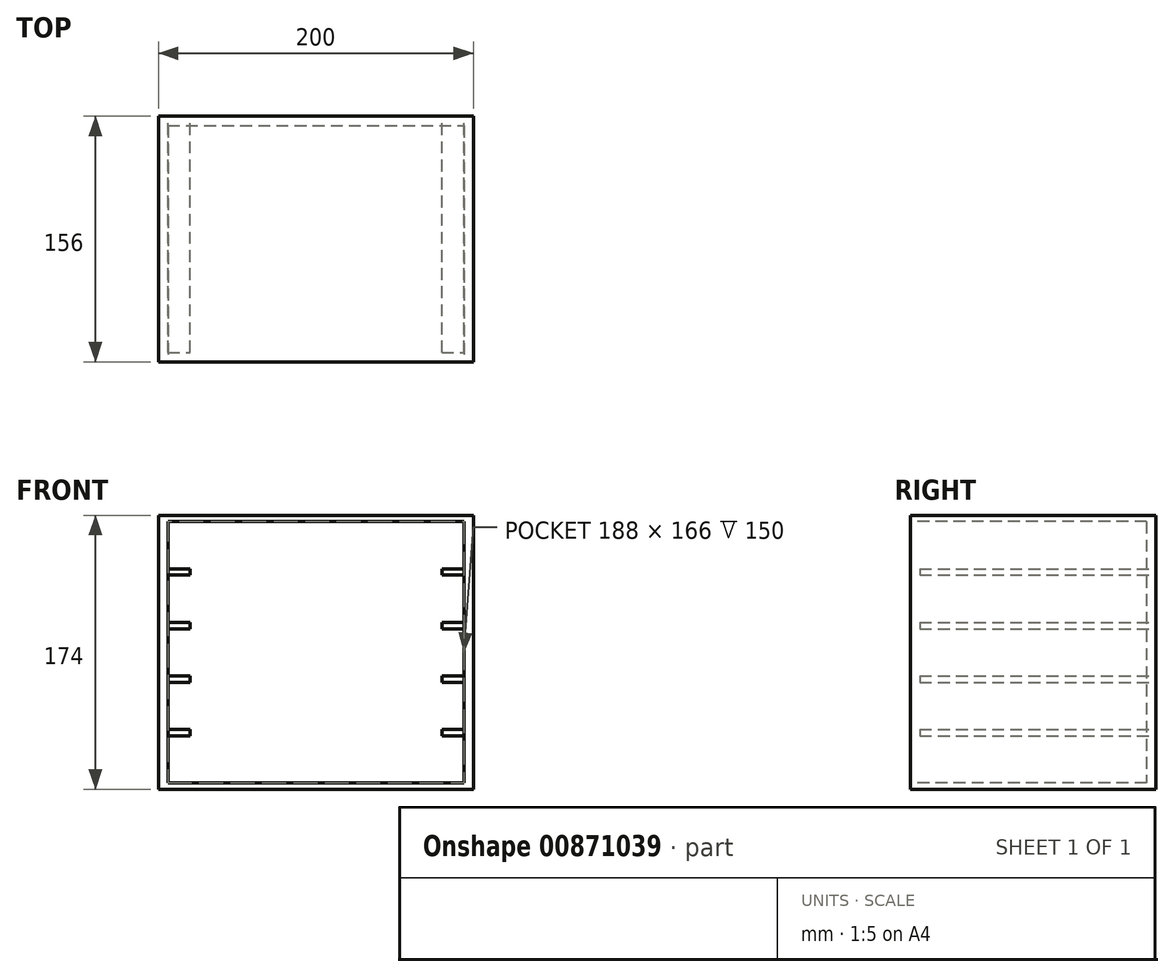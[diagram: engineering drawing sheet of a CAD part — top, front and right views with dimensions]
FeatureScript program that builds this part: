
annotation { "Feature Type Name" : "Feature", "Feature Type Description" : "" }
export const myFeature = defineFeature(function(context is Context, id is Id, definition is map)
    precondition{}
    {
        {
            var Q0;
            Q0=qCreatedBy(makeId("Front.planeOp"),FACE);
            var sketch = newSketch(context, id + "F0", { "sketchPlane" : qUnion([Q0])});
            skLineSegment(sketch, "E0.bottom", {"start": v(-100, 87) * mm, "end": v(100, 87) * mm});
            skLineSegment(sketch, "E0.top", {"start": v(-100, -87) * mm, "end": v(100, -87) * mm});
            skLineSegment(sketch, "E0.left", {"start": v(-100, 87) * mm, "end": v(-100, -87) * mm});
            skLineSegment(sketch, "E0.right", {"start": v(100, 87) * mm, "end": v(100, -87) * mm});
            skSolve(sketch);
        }
        {
            var Q0;
            Q0=makeQuery(id+"F0.imprint","IMPRINT",FACE,{"disambiguationData":[TD([[makeQuery(id+"F0.imprint","IMPRINT",EDGE,{"derivedFrom":sQuery(id+"F0.wireOp",EDGE,"E0.bottom")}),-1.0]])]});
            extrude(context, id + "F1", {"entities" : qUnion([Q0]), "depth" : 156 * mm, "offsetDistance" : 25 * mm});
        }
        {
            var Q0;
            Q0=makeQuery(id+"F1.opExtrude","CAP_FACE",FACE,{"disambiguationData":[OSD([sQuery(id+"F0.wireOp",EDGE,"E0.bottom"),sQuery(id+"F0.wireOp",EDGE,"E0.top"),sQuery(id+"F0.wireOp",EDGE,"E0.left"),sQuery(id+"F0.wireOp",EDGE,"E0.right")])],"isStart":false});
            var sketch = newSketch(context, id + "F2", { "sketchPlane" : qUnion([Q0])});
            skLineSegment(sketch, "E1.bottom", {"start": v(-94, 83) * mm, "end": v(94, 83) * mm});
            skLineSegment(sketch, "E1.top", {"start": v(-94, -83) * mm, "end": v(94, -83) * mm});
            skLineSegment(sketch, "E1.left", {"start": v(-94, 83) * mm, "end": v(-94, -83) * mm});
            skLineSegment(sketch, "E1.right", {"start": v(94, 83) * mm, "end": v(94, -83) * mm});
            skSolve(sketch);
        }
        {
            var Q0;
            Q0 = qSketchRegion(id + "F2", true);
            extrude(context, id + "F3", {"entities" : qUnion([Q0]), "operationType" : NewBodyOperationType.REMOVE, "oppositeDirection" : true, "depth" : 150 * mm, "offsetDistance" : 25 * mm});
        }
        {
            var Q0;
            Q0=qCreatedBy(makeId("Front.planeOp"),FACE);
            var sketch = newSketch(context, id + "F4", { "sketchPlane" : qUnion([Q0])});
            skLineSegment(sketch, "E2.bottom", {"start": v(-94, 83) * mm, "end": v(94, 83) * mm});
            skLineSegment(sketch, "E2.top", {"start": v(-94, -83) * mm, "end": v(94, -83) * mm});
            skLineSegment(sketch, "E2.left", {"start": v(-94, 83) * mm, "end": v(-94, -83) * mm});
            skLineSegment(sketch, "E2.right", {"start": v(94, 83) * mm, "end": v(94, -83) * mm});
            skLineSegment(sketch, "E3.bottom", {"start": v(-94, -83) * mm, "end": v(-80, -83) * mm});
            skLineSegment(sketch, "E3.top", {"start": v(-94, -87) * mm, "end": v(-80, -87) * mm});
            skLineSegment(sketch, "E3.left", {"start": v(-94, -83) * mm, "end": v(-94, -87) * mm});
            skLineSegment(sketch, "E3.right", {"start": v(-80, -83) * mm, "end": v(-80, -87) * mm});
            skLineSegment(sketch, "E4.0.1.0", {"start": v(-94, -53) * mm, "end": v(-80, -53) * mm});
            skLineSegment(sketch, "E4.0.1.1", {"start": v(-80, -49) * mm, "end": v(-80, -53) * mm});
            skLineSegment(sketch, "E4.0.1.2", {"start": v(-94, -49) * mm, "end": v(-80, -49) * mm});
            skLineSegment(sketch, "E4.0.1.3", {"start": v(-94, -49) * mm, "end": v(-94, -53) * mm});
            skLineSegment(sketch, "E4.0.2.0", {"start": v(-94, -19) * mm, "end": v(-80, -19) * mm});
            skLineSegment(sketch, "E4.0.2.1", {"start": v(-80, -15) * mm, "end": v(-80, -19) * mm});
            skLineSegment(sketch, "E4.0.2.2", {"start": v(-94, -15) * mm, "end": v(-80, -15) * mm});
            skLineSegment(sketch, "E4.0.2.3", {"start": v(-94, -15) * mm, "end": v(-94, -19) * mm});
            skLineSegment(sketch, "E4.0.3.0", {"start": v(-94, 15) * mm, "end": v(-80, 15) * mm});
            skLineSegment(sketch, "E4.0.3.1", {"start": v(-80, 19) * mm, "end": v(-80, 15) * mm});
            skLineSegment(sketch, "E4.0.3.2", {"start": v(-94, 19) * mm, "end": v(-80, 19) * mm});
            skLineSegment(sketch, "E4.0.3.3", {"start": v(-94, 19) * mm, "end": v(-94, 15) * mm});
            skLineSegment(sketch, "E4.0.4.0", {"start": v(-94, 49) * mm, "end": v(-80, 49) * mm});
            skLineSegment(sketch, "E4.0.4.1", {"start": v(-80, 53) * mm, "end": v(-80, 49) * mm});
            skLineSegment(sketch, "E4.0.4.2", {"start": v(-94, 53) * mm, "end": v(-80, 53) * mm});
            skLineSegment(sketch, "E4.0.4.3", {"start": v(-94, 53) * mm, "end": v(-94, 49) * mm});
            skLineSegment(sketch, "E4.1.0.0", {"start": v(80, -87) * mm, "end": v(94, -87) * mm});
            skLineSegment(sketch, "E4.1.0.1", {"start": v(94, -83) * mm, "end": v(94, -87) * mm});
            skLineSegment(sketch, "E4.1.0.2", {"start": v(80, -83) * mm, "end": v(94, -83) * mm});
            skLineSegment(sketch, "E4.1.0.3", {"start": v(80, -83) * mm, "end": v(80, -87) * mm});
            skLineSegment(sketch, "E4.1.1.0", {"start": v(80, -53) * mm, "end": v(94, -53) * mm});
            skLineSegment(sketch, "E4.1.1.1", {"start": v(94, -49) * mm, "end": v(94, -53) * mm});
            skLineSegment(sketch, "E4.1.1.2", {"start": v(80, -49) * mm, "end": v(94, -49) * mm});
            skLineSegment(sketch, "E4.1.1.3", {"start": v(80, -49) * mm, "end": v(80, -53) * mm});
            skLineSegment(sketch, "E4.1.2.0", {"start": v(80, -19) * mm, "end": v(94, -19) * mm});
            skLineSegment(sketch, "E4.1.2.1", {"start": v(94, -15) * mm, "end": v(94, -19) * mm});
            skLineSegment(sketch, "E4.1.2.2", {"start": v(80, -15) * mm, "end": v(94, -15) * mm});
            skLineSegment(sketch, "E4.1.2.3", {"start": v(80, -15) * mm, "end": v(80, -19) * mm});
            skLineSegment(sketch, "E4.1.3.0", {"start": v(80, 15) * mm, "end": v(94, 15) * mm});
            skLineSegment(sketch, "E4.1.3.1", {"start": v(94, 19) * mm, "end": v(94, 15) * mm});
            skLineSegment(sketch, "E4.1.3.2", {"start": v(80, 19) * mm, "end": v(94, 19) * mm});
            skLineSegment(sketch, "E4.1.3.3", {"start": v(80, 19) * mm, "end": v(80, 15) * mm});
            skLineSegment(sketch, "E4.1.4.0", {"start": v(80, 49) * mm, "end": v(94, 49) * mm});
            skLineSegment(sketch, "E4.1.4.1", {"start": v(94, 53) * mm, "end": v(94, 49) * mm});
            skLineSegment(sketch, "E4.1.4.2", {"start": v(80, 53) * mm, "end": v(94, 53) * mm});
            skLineSegment(sketch, "E4.1.4.3", {"start": v(80, 53) * mm, "end": v(80, 49) * mm});
            skLineSegment(sketch, "E4.direction1", {"start": v(-94, -87) * mm, "end": v(80, -87) * mm, "construction": true});
            skLineSegment(sketch, "E4.direction2", {"start": v(-94, -87) * mm, "end": v(-94, -53) * mm, "construction": true});
            skSolve(sketch);
        }
        {
            var Q0;
            Q0=makeQuery(id+"F4.imprint","IMPRINT",FACE,{"disambiguationData":[TD([[makeQuery(id+"F4.imprint","IMPRINT",EDGE,{"derivedFrom":sQuery(id+"F4.wireOp",EDGE,"E4.0.4.0")}),1.0]])]});
            var Q1;
            Q1=makeQuery(id+"F4.imprint","IMPRINT",FACE,{"disambiguationData":[TD([[makeQuery(id+"F4.imprint","IMPRINT",EDGE,{"derivedFrom":sQuery(id+"F4.wireOp",EDGE,"E4.0.3.0")}),1.0]])]});
            var Q2;
            Q2=makeQuery(id+"F4.imprint","IMPRINT",FACE,{"disambiguationData":[TD([[makeQuery(id+"F4.imprint","IMPRINT",EDGE,{"derivedFrom":sQuery(id+"F4.wireOp",EDGE,"E4.0.2.0")}),1.0]])]});
            var Q3;
            Q3=makeQuery(id+"F4.imprint","IMPRINT",FACE,{"disambiguationData":[TD([[makeQuery(id+"F4.imprint","IMPRINT",EDGE,{"derivedFrom":sQuery(id+"F4.wireOp",EDGE,"E4.0.1.0")}),1.0]])]});
            var Q4;
            Q4=makeQuery(id+"F4.imprint","IMPRINT",FACE,{"disambiguationData":[TD([[makeQuery(id+"F4.imprint","IMPRINT",EDGE,{"derivedFrom":sQuery(id+"F4.wireOp",EDGE,"E4.1.1.0")}),1.0]])]});
            var Q5;
            Q5=makeQuery(id+"F4.imprint","IMPRINT",FACE,{"disambiguationData":[TD([[makeQuery(id+"F4.imprint","IMPRINT",EDGE,{"derivedFrom":sQuery(id+"F4.wireOp",EDGE,"E4.1.2.0")}),1.0]])]});
            var Q6;
            Q6=makeQuery(id+"F4.imprint","IMPRINT",FACE,{"disambiguationData":[TD([[makeQuery(id+"F4.imprint","IMPRINT",EDGE,{"derivedFrom":sQuery(id+"F4.wireOp",EDGE,"E4.1.3.0")}),1.0]])]});
            var Q7;
            Q7=makeQuery(id+"F4.imprint","IMPRINT",FACE,{"disambiguationData":[TD([[makeQuery(id+"F4.imprint","IMPRINT",EDGE,{"derivedFrom":sQuery(id+"F4.wireOp",EDGE,"E4.1.4.0")}),1.0]])]});
            extrude(context, id + "F5", {"entities" : qUnion([Q0, Q1, Q2, Q3, Q4, Q5, Q6, Q7]), "depth" : 150 * mm, "offsetDistance" : 25 * mm});
        }
    });
